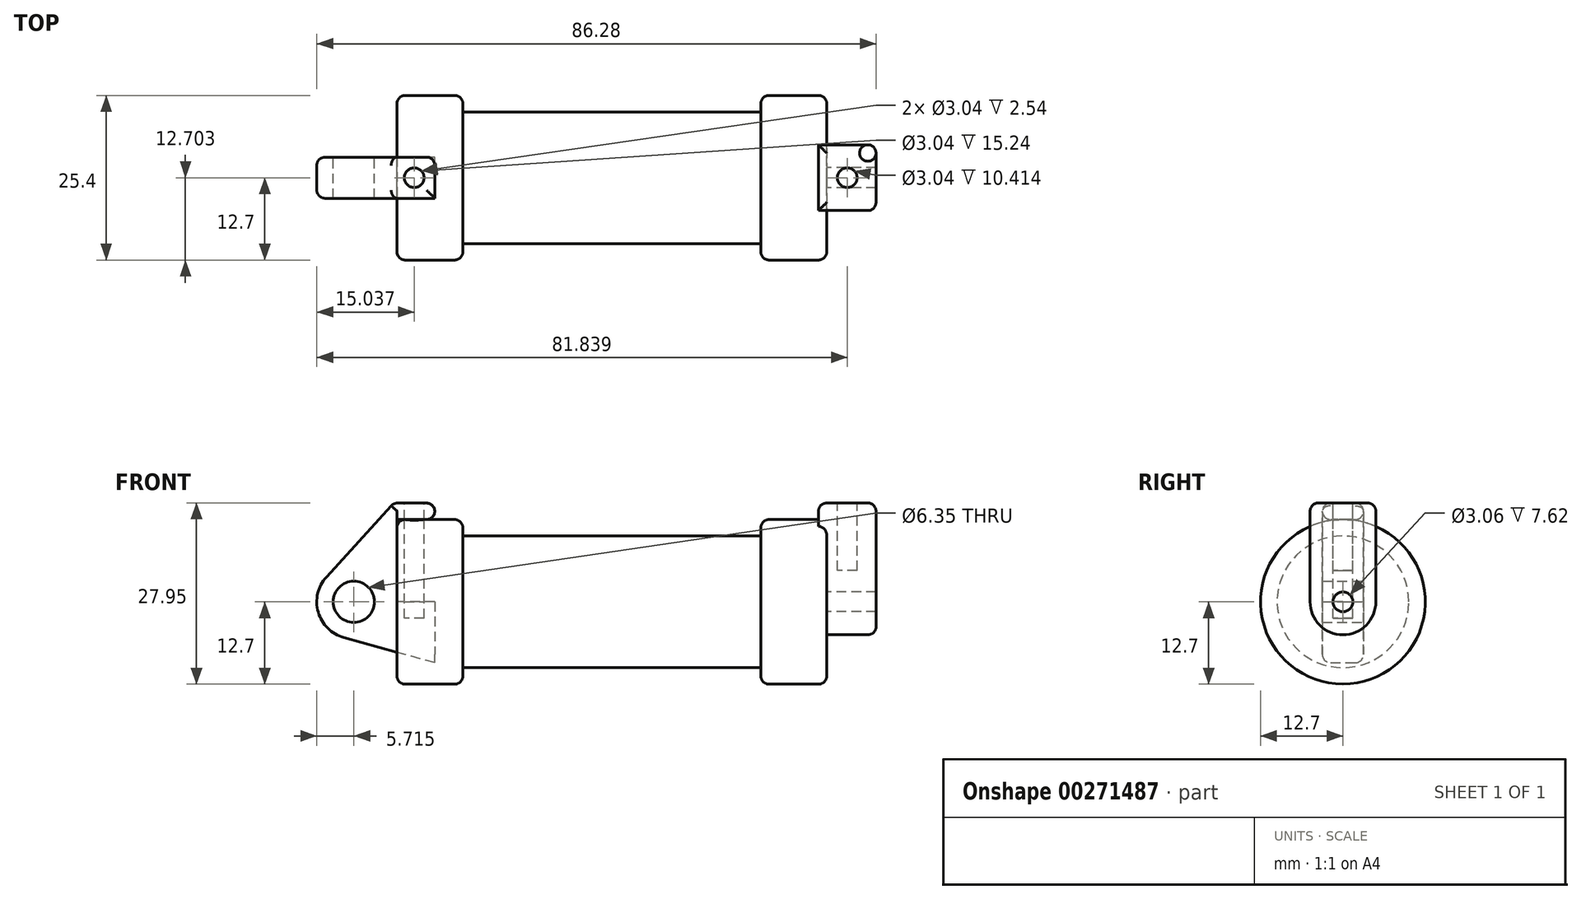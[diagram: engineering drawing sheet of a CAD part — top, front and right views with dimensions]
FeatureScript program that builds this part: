
annotation { "Feature Type Name" : "Feature", "Feature Type Description" : "" }
export const myFeature = defineFeature(function(context is Context, id is Id, definition is map)
    precondition{}
    {
        {
            var Q0;
            Q0=qCreatedBy(makeId("Front.planeOp"),FACE);
            var sketch = newSketch(context, id + "F0", { "sketchPlane" : qUnion([Q0])});
            skLineSegment(sketch, "E0", {"start": v(0, 0) * mm, "end": v(0, 12.7) * mm});
            skLineSegment(sketch, "E1", {"start": v(0, 12.7) * mm, "end": v(10.16, 12.7) * mm});
            skLineSegment(sketch, "E2", {"start": v(10.16, 12.7) * mm, "end": v(10.16, 10.16) * mm});
            skLineSegment(sketch, "E3", {"start": v(10.16, 10.16) * mm, "end": v(56.13, 10.16) * mm});
            skLineSegment(sketch, "E4", {"start": v(56.13, 10.16) * mm, "end": v(56.13, 12.7) * mm});
            skLineSegment(sketch, "E5", {"start": v(56.13, 12.7) * mm, "end": v(66.3, 12.7) * mm});
            skLineSegment(sketch, "E6", {"start": v(66.3, 12.7) * mm, "end": v(66.3, 0) * mm});
            skLineSegment(sketch, "E7", {"start": v(66.3, 0) * mm, "end": v(0, 0) * mm});
            skLineSegment(sketch, "E8", {"start": v(5.84, 15.24) * mm, "end": v(-0.5, 15.24) * mm});
            skLineSegment(sketch, "E9", {"start": v(-0.5, 15.24) * mm, "end": v(-10.88, 3.85) * mm});
            skLineSegment(sketch, "E10", {"start": v(0, 0) * mm, "end": v(-6.65, 0) * mm});
            skCircle(sketch, "E11", {"center": v(-6.65, 0) * mm, "radius": 5.72 * mm});
            skCircle(sketch, "E12", {"center": v(-6.65, 0) * mm, "radius": 3.18 * mm});
            skLineSegment(sketch, "E13", {"start": v(5.84, 15.24) * mm, "end": v(5.84, -9.4) * mm});
            skLineSegment(sketch, "E14", {"start": v(5.84, -9.4) * mm, "end": v(-8.18, -5.5) * mm});
            skSolve(sketch);
        }
        {
            var Q0;
            {var subQ0=sQuery(id+"F0.wireOp",EDGE,"E14");Q0=makeQuery(id+"F0.imprint","IMPRINT",FACE,{"disambiguationData":[TD([[makeQuery(id+"F0.imprint","IMPRINT",EDGE,{"derivedFrom":subQ0}),-1.0]])]});}
            var Q1;
            {var subQ3=sQuery(id+"F0.wireOp",EDGE,"E0");Q1=makeQuery(id+"F0.imprint","IMPRINT",FACE,{"disambiguationData":[TD([[makeQuery(id+"F0.imprint","IMPRINT",EDGE,{"derivedFrom":subQ3}),1.0]])]});}
            var Q2;
            {var subQ4=sQuery(id+"F0.wireOp",EDGE,"E12");Q2=makeQuery(id+"F0.imprint","IMPRINT",FACE,{"disambiguationData":[TD([[makeQuery(id+"F0.imprint","IMPRINT",EDGE,{"derivedFrom":subQ4}),-1.0]])]});}
            extrude(context, id + "F1", {"entities" : qUnion([Q0, Q1, Q2]), "depth" : 6.35 * mm, "symmetric" : true});
        }
        {
            var Q0;
            {var subQ0=sQuery(id+"F0.wireOp",EDGE,"E0");Q0=makeQuery(id+"F0.imprint","IMPRINT",FACE,{"disambiguationData":[TD([[makeQuery(id+"F0.imprint","IMPRINT",EDGE,{"derivedFrom":subQ0}),-1.0]])]});}
            var Q1;
            {var subQ0=sQuery(id+"F0.wireOp",EDGE,"E2");Q1=makeQuery(id+"F0.imprint","IMPRINT",FACE,{"disambiguationData":[TD([[makeQuery(id+"F0.imprint","IMPRINT",EDGE,{"derivedFrom":subQ0}),-1.0]])]});}
            var Q2;
            Q2=sQuery(id+"F0.wireOp",EDGE,"E7");
            revolve(context, id + "F2", {"entities" : qUnion([Q0, Q1]), "axis" : qUnion([Q2]), "revolveType" : RevolveType.FULL});
        }
        {
            var Q0;
            Q0=makeQuery(id+"F2.opRevolve","SWEPT_FACE",FACE,{"disambiguationData":[OSD([sQuery(id+"F0.wireOp",EDGE,"E6")])]});
            var sketch = newSketch(context, id + "F3", { "sketchPlane" : qUnion([Q0])});
            skCircle(sketch, "E15", {"center": v(0, 0) * mm, "radius": 5.07 * mm});
            skCircle(sketch, "E16", {"center": v(0, 0) * mm, "radius": 1.53 * mm});
            skLineSegment(sketch, "E17", {"start": v(-5.07, 0) * mm, "end": v(-5.07, 15.25) * mm});
            skLineSegment(sketch, "E18", {"start": v(-5.07, 15.25) * mm, "end": v(5.08, 15.25) * mm});
            skLineSegment(sketch, "E19", {"start": v(5.08, 15.25) * mm, "end": v(5.07, 0) * mm});
            skSolve(sketch);
        }
        {
            var Q0;
            {var subQ0=sQuery(id+"F3.wireOp",EDGE,"E18");Q0=makeQuery(id+"F3.imprint","IMPRINT",FACE,{"disambiguationData":[TD([[makeQuery(id+"F3.imprint","IMPRINT",EDGE,{"derivedFrom":subQ0}),-1.0]])]});}
            var Q1;
            {var subQ0=sQuery(id+"F3.wireOp",EDGE,"E17");var subQ1=sQuery(id+"F3.wireOp",EDGE,"E15");var subQ2=makeQuery(id+"F3.imprint","INTERSECT",VERTEX,{"derivedFrom":[subQ1,subQ0]});Q1=makeQuery(id+"F3.imprint","IMPRINT",FACE,{"disambiguationData":[TD([[makeQuery(id+"F3.imprint","IMPRINT",EDGE,{"disambiguationData":[TD([[subQ2,1.0]])],"derivedFrom":subQ1}),-1.0]])]});}
            var Q2;
            Q2=makeQuery(id+"F3.imprint","IMPRINT",FACE,{"disambiguationData":[TD([[makeQuery(id+"F3.imprint","IMPRINT",EDGE,{"derivedFrom":sQuery(id+"F3.wireOp",EDGE,"E16")}),-1.0]])]});
            extrude(context, id + "F4", {"entities" : qUnion([Q0, Q1, Q2]), "operationType" : NewBodyOperationType.ADD, "depth" : 7.62 * mm});
        }
        {
            var Q0;
            Q0=makeQuery(id+"F4.opExtrude","CAP_FACE",FACE,{"disambiguationData":[OSD([sQuery(id+"F3.wireOp",EDGE,"E15"),sQuery(id+"F3.wireOp",EDGE,"E16"),sQuery(id+"F3.wireOp",EDGE,"E17"),sQuery(id+"F3.wireOp",EDGE,"E18"),sQuery(id+"F3.wireOp",EDGE,"E19")])],"isStart":true});
            extrude(context, id + "F5", {"entities" : qUnion([Q0]), "operationType" : NewBodyOperationType.ADD, "depth" : 1.27 * mm});
        }
        {
            var Q0;
            Q0=makeQuery(id+"F1.opExtrude","SWEPT_FACE",FACE,{"disambiguationData":[OSD([sQuery(id+"F0.wireOp",EDGE,"E8")])]});
            var sketch = newSketch(context, id + "F6", { "sketchPlane" : qUnion([Q0])});
            skCircle(sketch, "E20", {"center": v(2.67, 0) * mm, "radius": 1.52 * mm});
            skPoint(sketch, "E20.centerSnap0", {"position": v(2.67, -3.18) * mm});
            skPoint(sketch, "E20.centerSnap1", {"position": v(5.84, 0) * mm});
            skSolve(sketch);
        }
        {
            var Q0;
            Q0=makeQuery(id+"F6.imprint","IMPRINT",FACE,{"disambiguationData":[TD([[makeQuery(id+"F6.imprint","IMPRINT",EDGE,{"derivedFrom":sQuery(id+"F6.wireOp",EDGE,"E20")}),1.0]])]});
            var Q1;
            Q1=sQuery(id+"F6.wireOp",EDGE,"E20");
            extrude(context, id + "F7", {"entities" : qUnion([Q0]), "operationType" : NewBodyOperationType.REMOVE, "surfaceEntities" : qUnion([Q1]), "oppositeDirection" : true, "depth" : 17.78 * mm});
        }
        {
            var Q0;
            {var subQ0=sQuery(id+"F3.wireOp",EDGE,"E18");Q0=makeQuery(id+"F5.boolean.opBoolean","MERGE",FACE,{"derivedFrom":[makeQuery(id+"F4.opExtrude","SWEPT_FACE",FACE,{"disambiguationData":[OSD([subQ0])]}),makeQuery(id+"F5.opExtrude","SWEPT_FACE",FACE,{"disambiguationData":[OSD([subQ0])]})]});}
            var sketch = newSketch(context, id + "F8", { "sketchPlane" : qUnion([Q0])});
            skCircle(sketch, "E21", {"center": v(69.47, 0) * mm, "radius": 1.52 * mm});
            skSolve(sketch);
        }
        {
            var Q0;
            Q0=makeQuery(id+"F8.imprint","IMPRINT",FACE,{"disambiguationData":[TD([[makeQuery(id+"F8.imprint","IMPRINT",EDGE,{"derivedFrom":sQuery(id+"F8.wireOp",EDGE,"E21")}),1.0]])]});
            extrude(context, id + "F9", {"entities" : qUnion([Q0]), "operationType" : NewBodyOperationType.REMOVE, "oppositeDirection" : true, "depth" : 10.4 * mm});
        }
        {
            var Q0;
            Q0=makeQuery(id+"F2.opRevolve","SWEPT_EDGE",EDGE,{"disambiguationData":[OSD([sQuery(id+"F0.wireOp",EDGE,"E1"),sQuery(id+"F0.wireOp",EDGE,"E2")])]});
            var Q1;
            Q1=makeQuery(id+"F2.opRevolve","SWEPT_EDGE",EDGE,{"disambiguationData":[OSD([sQuery(id+"F0.wireOp",EDGE,"E0"),sQuery(id+"F0.wireOp",EDGE,"E1")])]});
            var Q2;
            Q2=makeQuery(id+"F2.opRevolve","SWEPT_EDGE",EDGE,{"disambiguationData":[OSD([sQuery(id+"F0.wireOp",EDGE,"E4"),sQuery(id+"F0.wireOp",EDGE,"E5")])]});
            var Q3;
            Q3=makeQuery(id+"F4.boolean.opBoolean","SPLIT",EDGE,{"disambiguationData":[OD(1.0)],"derivedFrom":makeQuery(id+"F2.opRevolve","SWEPT_EDGE",EDGE,{"disambiguationData":[OSD([sQuery(id+"F0.wireOp",EDGE,"E5"),sQuery(id+"F0.wireOp",EDGE,"E6")])]})});
            var Q4;
            Q4=makeQuery(id+"F1.opExtrude","CAP_EDGE",EDGE,{"disambiguationData":[OSD([sQuery(id+"F0.wireOp",EDGE,"E14")])],"isStart":false});
            var Q5;
            Q5=makeQuery(id+"F1.opExtrude","CAP_EDGE",EDGE,{"disambiguationData":[OSD([sQuery(id+"F0.wireOp",EDGE,"E9")])],"isStart":true});
            var Q6;
            Q6=makeQuery(id+"F5.opExtrude","CAP_EDGE",EDGE,{"disambiguationData":[OSD([sQuery(id+"F0.wireOp",EDGE,"E5"),sQuery(id+"F0.wireOp",EDGE,"E6")])],"isStart":false});
            var Q7;
            Q7=makeQuery(id+"F5.opExtrude","CAP_EDGE",EDGE,{"disambiguationData":[OSD([sQuery(id+"F3.wireOp",EDGE,"E18")])],"isStart":false});
            var Q8;
            {var subQ0=sQuery(id+"F3.wireOp",EDGE,"E18");var subQ1=sQuery(id+"F3.wireOp",EDGE,"E17");Q8=makeQuery(id+"F5.boolean.opBoolean","MERGE",EDGE,{"derivedFrom":[makeQuery(id+"F4.opExtrude","SWEPT_EDGE",EDGE,{"disambiguationData":[OSD([subQ1,subQ0])]}),makeQuery(id+"F5.opExtrude","SWEPT_EDGE",EDGE,{"disambiguationData":[OSD([subQ1,subQ0])]})]});}
            var Q9;
            Q9=makeQuery(id+"F4.opExtrude","CAP_EDGE",EDGE,{"disambiguationData":[OSD([sQuery(id+"F3.wireOp",EDGE,"E18")])],"isStart":false});
            var Q10;
            {var subQ0=sQuery(id+"F3.wireOp",EDGE,"E19");var subQ1=sQuery(id+"F3.wireOp",EDGE,"E18");Q10=makeQuery(id+"F5.boolean.opBoolean","MERGE",EDGE,{"derivedFrom":[makeQuery(id+"F4.opExtrude","SWEPT_EDGE",EDGE,{"disambiguationData":[OSD([subQ1,subQ0])]}),makeQuery(id+"F5.opExtrude","SWEPT_EDGE",EDGE,{"disambiguationData":[OSD([subQ1,subQ0])]})]});}
            var Q11;
            Q11=makeQuery(id+"F4.opExtrude","CAP_EDGE",EDGE,{"disambiguationData":[OSD([sQuery(id+"F3.wireOp",EDGE,"E17")])],"isStart":false});
            fillet(context, id + "F10", {"entities" : qUnion([Q0, Q1, Q2, Q3, Q4, Q5, Q6, Q7, Q8, Q9, Q10, Q11]), "radius" : 1.27 * mm, "tangentPropagation" : true, "allowEdgeOverflow" : false});
        }
        {
            var Q0;
            {var subQ0=sQuery(id+"F3.wireOp",EDGE,"E17");var subQ1=sQuery(id+"F3.wireOp",EDGE,"E15");Q0=makeQuery(id+"F4.boolean.opBoolean","SPLIT",EDGE,{"disambiguationData":[TD([makeQuery(id+"F4.opExtrude","SWEPT_FACE",FACE,{"disambiguationData":[OSD([subQ1])]})])],"derivedFrom":makeQuery(id+"F4.opExtrude","CAP_EDGE",EDGE,{"disambiguationData":[OSD([subQ0])],"isStart":true})});}
            var Q1;
            {var subQ0=sQuery(id+"F0.wireOp",EDGE,"E14");Q1=makeQuery(id+"F10.opFillet","BLEND_EDGE",EDGE,{"blendedFrom":[makeQuery(id+"F1.opExtrude","CAP_EDGE",EDGE,{"disambiguationData":[OSD([subQ0])],"isStart":true}),makeQuery(id+"F1.opExtrude","CAP_FACE",FACE,{"disambiguationData":[OSD([sQuery(id+"F0.wireOp",EDGE,"E0"),sQuery(id+"F0.wireOp",EDGE,"E1"),sQuery(id+"F0.wireOp",EDGE,"E7"),sQuery(id+"F0.wireOp",EDGE,"E8"),sQuery(id+"F0.wireOp",EDGE,"E9"),sQuery(id+"F0.wireOp",EDGE,"E11"),sQuery(id+"F0.wireOp",EDGE,"E12"),sQuery(id+"F0.wireOp",EDGE,"E13"),subQ0])],"isStart":true})],"blendedInto":[makeQuery(id+"F1.opExtrude","CAP_FACE",FACE,{"disambiguationData":[OSD([sQuery(id+"F0.wireOp",EDGE,"E0"),sQuery(id+"F0.wireOp",EDGE,"E1"),sQuery(id+"F0.wireOp",EDGE,"E7"),sQuery(id+"F0.wireOp",EDGE,"E8"),sQuery(id+"F0.wireOp",EDGE,"E9"),sQuery(id+"F0.wireOp",EDGE,"E11"),sQuery(id+"F0.wireOp",EDGE,"E12"),sQuery(id+"F0.wireOp",EDGE,"E13"),subQ0])],"isStart":true})]});}
            var Q2;
            Q2=makeQuery(id+"F1.opExtrude","CAP_EDGE",EDGE,{"disambiguationData":[OSD([sQuery(id+"F0.wireOp",EDGE,"E1")])],"isStart":true});
            var Q3;
            Q3=makeQuery(id+"F1.opExtrude","CAP_EDGE",EDGE,{"disambiguationData":[OSD([sQuery(id+"F0.wireOp",EDGE,"E8")])],"isStart":true});
            var Q4;
            Q4=makeQuery(id+"F1.opExtrude","SWEPT_EDGE",EDGE,{"disambiguationData":[OSD([sQuery(id+"F0.wireOp",EDGE,"E1"),sQuery(id+"F0.wireOp",EDGE,"E13")])]});
            var Q5;
            Q5=makeQuery(id+"F1.opExtrude","SWEPT_EDGE",EDGE,{"disambiguationData":[OSD([sQuery(id+"F0.wireOp",EDGE,"E8"),sQuery(id+"F0.wireOp",EDGE,"E13")])]});
            var Q6;
            {var subQ0=sQuery(id+"F0.wireOp",EDGE,"E13");Q6=makeQuery(id+"F1.opExtrude","CAP_EDGE",EDGE,{"disambiguationData":[OSD([subQ0]),TDD([makeQuery(id+"F0.imprint","IMPRINT",EDGE,{"disambiguationData":[TD([[makeQuery(id+"F0.imprint","INTERSECT",VERTEX,{"derivedFrom":[sQuery(id+"F0.wireOp",EDGE,"E8"),subQ0]}),-1.0]])],"derivedFrom":subQ0})])],"isStart":true});}
            var Q7;
            Q7=makeQuery(id+"F1.opExtrude","CAP_EDGE",EDGE,{"disambiguationData":[OSD([sQuery(id+"F0.wireOp",EDGE,"E1")])],"isStart":false});
            fillet(context, id + "F11", {"entities" : qUnion([Q0, Q1, Q2, Q3, Q4, Q5, Q6, Q7]), "radius" : 1.27 * mm, "tangentPropagation" : true, "allowEdgeOverflow" : false});
        }
    });
